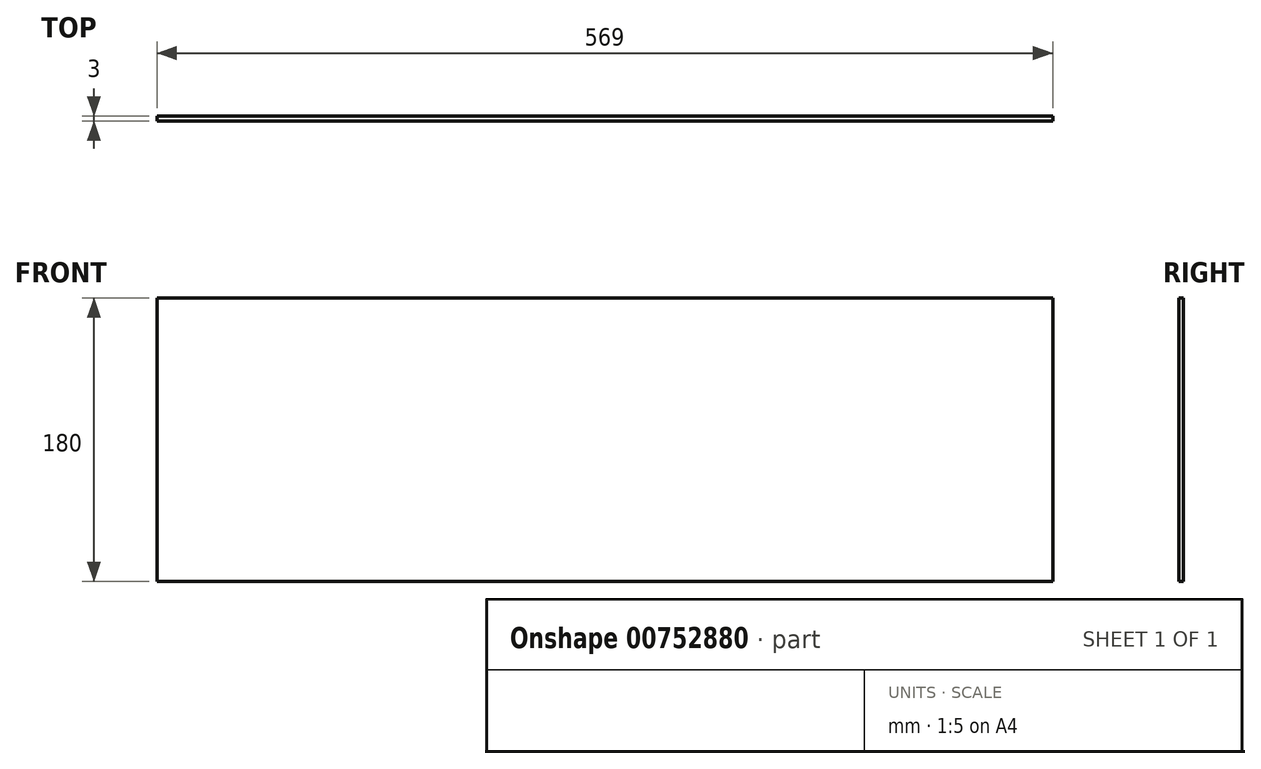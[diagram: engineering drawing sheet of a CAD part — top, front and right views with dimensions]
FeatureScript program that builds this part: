
annotation { "Feature Type Name" : "Feature", "Feature Type Description" : "" }
export const myFeature = defineFeature(function(context is Context, id is Id, definition is map)
    precondition{}
    {
        {
            var Q0;
            Q0=qCreatedBy(makeId("Front.planeOp"),FACE);
            var sketch = newSketch(context, id + "F0", { "sketchPlane" : qUnion([Q0])});
            skLineSegment(sketch, "E0.bottom", {"start": v(-284.5, 90) * mm, "end": v(284.5, 90) * mm});
            skLineSegment(sketch, "E0.top", {"start": v(-284.5, -90) * mm, "end": v(284.5, -90) * mm});
            skLineSegment(sketch, "E0.left", {"start": v(-284.5, 90) * mm, "end": v(-284.5, -90) * mm});
            skLineSegment(sketch, "E0.right", {"start": v(284.5, 90) * mm, "end": v(284.5, -90) * mm});
            skPoint(sketch, "E0.middle", {"position": v(0, 0) * mm});
            skSolve(sketch);
        }
        {
            var Q0;
            Q0=makeQuery(id+"F0.imprint","IMPRINT",FACE,{"disambiguationData":[TD([[makeQuery(id+"F0.imprint","IMPRINT",EDGE,{"derivedFrom":sQuery(id+"F0.wireOp",EDGE,"E0.bottom")}),-1.0]])]});
            extrude(context, id + "F1", {"entities" : qUnion([Q0]), "depth" : 3 * mm, "offsetDistance" : 25 * mm});
        }
    });
